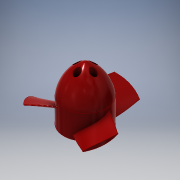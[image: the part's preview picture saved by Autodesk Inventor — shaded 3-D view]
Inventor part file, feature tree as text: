
AUTODESK INVENTOR PART (.ipt)
format: ipt  version: 2017 (Build 210142000, 142)  size: 522,752 bytes
history: native  units: mm
features: sketch x15, extrude x11, other x9, projected_geometry x5, plane x3, revolve x2, pattern_circular x2, loft x1, boolean_combine x1, fillet x1
ambient origin geometry x8: Origin, YZ Plane, XZ Plane, XY Plane, X Axis, Y Axis, Z Axis, Center Point
bodies: Body (feature_tree)
feature tree (50):
  other  "CrossSection1"
  other  "CrossSection2"
  other  "CrossSection3"
  other  "CrossSection4"
  other  "CrossSection5"
  other  "CrossSection6"
  other  "CrossSection7"
  extrude  "Extrusion1"  Depth=2.0mm
  revolve  "Revolution1"  Angle=90.0deg
  plane  "Work Plane2"
  sketch  "Sketch4"  dims[d6=40.0mm d7=1.0mm]
  plane  "Work Plane1"
  sketch  "Sketch5"  dims[d18=35.0mm]
  loft  "Loft1"
  pattern_circular  "Circular Pattern1"  Count=4  [1 undecoded]
  extrude  "Extrusion5"  Depth=21.7mm TaperAngle=0.0deg
  extrude  "Extrusion6"  Depth=2.5mm
  plane  "Work Plane3"
  extrude  "Extrusion7"  Depth=4.0mm TaperAngle=0.0deg
  extrude  "Extrusion8"  Depth=6.0mm
  extrude  "Extrusion9"  Depth=3.0mm TaperAngle=0.0deg
  pattern_circular  "Circular Pattern2"  [2 undecoded]
  extrude  "Extrusion10"  Depth=3.0mm TaperAngle=0.0deg
  extrude  "Extrusion11"  Depth=40.0mm TaperAngle=360.0deg
  boolean_combine  "Combine1"
  fillet  "Fillet2"  Radius=3.56mm
  extrude  "Extrusion12"  Depth=16.5mm TaperAngle=0.0deg
  extrude  "Extrusion13"  Depth=9.27mm
  extrude  "Extrusion14"  Depth=2.5mm TaperAngle=0.0deg
  revolve  "Revolution2"  [1 undecoded]
  sketch  "Sketch1"  dims[d0=28.1mm d1=2.0mm]
  sketch  "Sketch2"  dims[d2=18.0mm d3=0.0mm d5=90.0deg]
  projected_geometry  "Projected Loop1"
  projected_geometry  "Projected Loop2"
  other  "Cone"
  projected_geometry  "Projected Loop5"
  projected_geometry  "Projected Loop6"
  sketch  "Sketch7"  dims[d22=30.0deg]
  sketch  "Sketch8"  dims[d23=3.5mm]
  sketch  "Sketch9"  dims[d24=0.0mm d25=90.0deg d26=0.0mm d27=90.0deg d28=9.5mm]
  sketch  "Sketch10"  dims[d29=60.0deg]
  sketch  "Sketch11"  dims[d31=22.0mm]
  sketch  "Sketch12"  dims[d37=65.0mm]
  sketch  "Sketch13"  dims[d38=12.0mm d39=40.0mm d40=0.0mm]
  sketch  "Sketch14"  dims[d42=30.0mm d43=360.0deg d48=21.7mm d49=0.0mm]
  sketch  "Sketch15"  dims[d50=5.0mm d51=2.5mm]
  projected_geometry  "Projected Loop8"
  other  "Support"
  sketch  "Sketch16"  dims[d52=-21.7mm d53=4.0mm d54=0.0mm]
  sketch  "Sketch17"  dims[d58=2.5mm d59=6.0mm d60=3.0mm d61=0.0mm d62=4.8mm d63=3.0mm d64=0.0mm d65=40.0mm d66=360.0deg d68=3.56mm d69=16.5mm d70=0.0mm d71=9.27mm d72=2.5mm d73=0.0mm d74=0.5mm d75=2.0mm d76=-3.75mm d77=20.0mm d78=0.5mm d79=2.0mm d80=0.0mm d81=20.0mm d82=0.5mm d83=2.0mm d84=0.0mm d85=20.0mm d86=0.5mm d87=2.0mm d88=0.0mm d89=20.0mm d90=0.5mm d91=2.0mm d92=0.0mm d93=20.0mm d94=0.5mm d95=2.0mm d96=0.0mm d97=20.0mm d98=0.3mm d99=0.2mm d100=0.0mm d101=0.5mm d102=2.0mm d103=-23.0mm d104=20.0mm d105=0.2mm d106=0.0mm d107=0.2mm d108=0.0mm d112=6.981317mm d113=4.0mm d114=90.0deg]
note: 4 required parameter values undecoded (feature->parameter linkage not recoverable at this tier; creation-order binding heuristic only, values carry confidence <= 0.55)